# Revit family: Chair-Soft_Seating-Allermuir-Conic-A634
name_source: partatom
category: Furniture
revit_build: Autodesk Revit MEP 2012 (Build: 20110309_2315)
units: mm (PartAtom-declared; Revit-internal decimal feet)

## types (1)
- A634
    04 CSI = 12 51 00
    95 CSI = 12510
    Assembly Code = E2020200
    Base = Metal - Allermuir - Chrome - Polished
    Description = Lounge chair, pedestal base
    Diameter = 0 "
    Glide Finish = Plastic - Allermuir - Black
    Manufacturer = Allermuir
    Manufacturer Fax = (419) 887 5805
    Model = A634
    Overall Depth = 32 "
    Overall Height = 0 "
    Overall Width = 36 "
    Pedestal Base = Yes
    Plastic Arms in Black = No
    Plugin Data URL = http://products.ecoscorecard.com
    Product Line = Conic
    Seat Depth = 21 "
    Seat Height = 0 "
    Seat Width = 21 "
    Seat or Top = Fabric - Allermuir - Silcoates
    Stacks = No
    Subcategory = Soft Seating
    Tubular Steel Legs = No
    URL = http://www.allermuir.net
    Upholstered Back = Yes
    Upholstered Seat = Yes
    Weight = 85.00 lb
    ecoScorecard Product Page = http://products.ecoscorecard.com
http://products.ecoscorecard.com
    ecoScorecard_data = http://thesenatorgroup.ecoscorecard.com

## geometry (parser evidence)
native form markers: Blend x9, Sweep x24
no freeform markers — native parametric forms only
